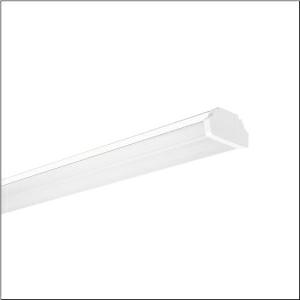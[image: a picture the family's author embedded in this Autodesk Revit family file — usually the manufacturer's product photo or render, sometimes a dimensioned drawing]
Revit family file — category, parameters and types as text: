
# Revit family: dus_r__31_mo_53bd812d2v4085_2fe7
name_source: partatom
category: Lighting Fixtures
units: mm (PartAtom-declared; Revit-internal decimal feet)

## family parameters
Cut with Voids When Loaded = No
Host = Face
Light Source = No
Part Type = Normal
Room Calculation Point = No
Round Connector Dimension = Use Diameter
Shared = No

## types (1)
- --- (1 x LED, 8930 lm, 61.8 W, 4000K)
    Apparent Load = 62 VA
    CIE Flux Codes = 47 80 95 92 100
    Color Rendering = 80
    Color Temperature = 4000K
    Default Elevation = 1800 mm
    Description = DUS® 31 MO, luminaire insert, of sheet steel, coil coated, white, length: 1.535mm, width: 81mm, height: 90mm, 5x system unit, system units: 307mm, LED rated luminous flux: 8.930lm, light colour: 840, control gear: DALI 2, control gear: ECG DALI, with plug, 5-pole, with phase selection, mains connection: 220..240V, AC, 50/60Hz, rated input power: 62W, through-wiring accessed according to module size, primary optical cover: cover, of PMMA, light emission: direct distribution, primary light characteristic: symmetric, protection rating (complete): IP20, protection rating (LED compartment): IP50, insulation class (complete): insulation class I (protective earthing), certification: CE, ENEC, VDE, UKCA, impact resistance: IK03, permissible ambient temperature for indoor applications: -25..+30°C, corresponds to IFS (International Featured Standards) requirements for safety and quality in the food industry, reducing of maximum allowable ambient temperature of 5°C with ceiling mounting, packaging unit: 1 piece
    Height = 95 mm
    Lamp = 1 x LED
    Lamp Light Flux = 8930 lm
    Lamp Power = 61.8 W
    Lamp count = 1
    Length = 1535 mm
    Luminous efficacy = 145 lm/W
    Manufacturer = Siteco
    ModVariant = No
    Model = 53BD812D2V4085
    Mounting Place = Ceiling
    Mounting Type = Pendant
    Number of Poles = 1
    OnlyDefault = Yes
    Power Factor = 1
    Product Name = DUS® 31 MO
    Product group = luminaire insert
    ProductGroupID = 901
    Protection Class = Protection class I
    Protection Degree = IP 20
    RLX_Detail_Level = 1
    RLX_Emergency_Light_Flux = 0 lm
    RLX_Emergency_Type = 0
    RLX_Emergency_Type_DB = No
    RlxData = <blob elided: 42069 chars, md5=1f4358fb>
    Socket = socket
    Standby Power = 0 W
    System Light Flux = 8930 lm
    System Power = 62 W
    Type Comments = factory setting: luminous flux: 100 % | dim-lin: 254 | 500 mA
    Type Image = l_1319596.jpg
    URL = http://relux.com
    VarID = @adj_168535
    Voltage = 0 V
    Weight = 0.00 kg
    Width = 81 mm

## geometry (parser evidence)
native form markers: Blend x4, Sweep x12
no freeform markers — native parametric forms only
